# Revit family: CRUo
name_source: partatom
category: Lighting Fixtures
units: mm (PartAtom-declared; Revit-internal decimal feet)

## family parameters
Always vertical = Yes
Cut with Voids When Loaded = No
Host = Ceiling
Light Source = Yes
Maintain Annotation Orientation = No
OmniClass Number = 23.80.70.11.14.17
OmniClass Title = Direct/Indirect
Part Type = Normal
Room Calculation Point = No
Round Connector Dimension = Use Diameter
Shared = No

## types (15) — shared parameters
Color Filter = 16777215
Default Elevation = 0' - 0"
Description = LED Cleanroom Recessed with Overlapping Doorframe
Dimming Lamp Color Temperature Shift = <None>
Emit Shape Visible in Rendering = No
Housing Finish = Metal - Viscor - White
Lamp = LED
Manufacturer = Certolux By Viscor
Model = CRUo
Tilt Angle = 90.00°
URL = https://viscor.com
Voltage = 120 V

## per-type parameters (varying)
| type | Apparent Load | Assembly Code | Emit from Rectangle Length | Emit from Rectangle Width | Lamp Wattage | Length | Lens Finish | Photometric Web File | Width |
| CRUo-1X4-LED840K035LUNV-DSA | 32 VA |  | 3' - 11 3/4" | 0' - 11 3/4" | 32 VA | 3' - 11 3/4" | Acrylic - Viscor - Frosted Prismatic P12 | CRUo-1X4-LED840K035LUNV-DSA.ies | 0' - 11 3/4" |
| CRUo-2X2-LED840K035LUNV-DSA | 31 VA |  | 1' - 11 3/4" | 1' - 11 3/4" | 31 VA | 1' - 11 3/4" | Acrylic - Viscor - Frosted Prismatic P12 | CRUo-2X2-LED840K035LUNV-DSA.ies | 1' - 11 3/4" |
| CRUo-2X4-LED840K055LUNV-DSA | 45 VA |  | 3' - 11 3/4" | 1' - 11 3/4" | 45 VA | 3' - 11 3/4" | Acrylic - Viscor - Frosted Prismatic P12 | CRUo-2X4-LED840K55LUNV-DSA.IES | 1' - 11 3/4" |
| CRUo-1X4-LED840K055LUNV-DSA | 51 VA |  | 3' - 11 3/4" | 0' - 11 3/4" | 51 VA | 3' - 11 3/4" | Acrylic - Viscor - Frosted Prismatic P12 | CRUo-1X4-LED840K055LUNV-DSA.ies | 0' - 11 3/4" |
| CRUo-1X4-LED840K070LUNV-DSA | 68 VA |  | 3' - 11 3/4" | 0' - 11 3/4" | 68 VA | 3' - 11 3/4" | Acrylic - Viscor - Frosted Prismatic P12 | CRUo-1X4-LED840K070LUNV-DSA.ies | 0' - 11 3/4" |
| CRUo-1X4-LED840K100LUNV-DSA | 96 VA | D5020200 | 3' - 11 3/4" | 0' - 11 3/4" | 96 VA | 3' - 11 3/4" | Acrylic - Viscor - Frosted Prismatic P12 | CRUo-1X4-LED840K100LUNV-DSA.ies | 0' - 11 3/4" |
| CRUo-2X2-LED840K055LUNV-DSA | 50 VA |  | 1' - 11 3/4" | 1' - 11 3/4" | 50 VA | 1' - 11 3/4" | Acrylic - Viscor - Frosted Prismatic P12 | CRUo-2X2-LED840K055LUNV-DSA.ies | 1' - 11 3/4" |
| CRUo-2X2-LED840K070LUNV-DSA | 65 VA |  | 1' - 11 3/4" | 1' - 11 3/4" | 65 VA | 1' - 11 3/4" | Acrylic - Viscor - Frosted Prismatic P12 | CRUo-2X2-LED840K070LUNV-DSA.ies | 1' - 11 3/4" |
| CRUo-2X2-LED840K100LUNV-DSA | 93 VA |  | 1' - 11 3/4" | 1' - 11 3/4" | 93 VA | 1' - 11 3/4" | Acrylic - Viscor - Frosted Prismatic P12 | CRUo-2X2-LED840K100LUNV-DSA.ies | 1' - 11 3/4" |
| CRUo-2X4-LED840K070LUNV-DSA | 59 VA |  | 3' - 11 3/4" | 1' - 11 3/4" | 59 VA | 3' - 11 3/4" | Acrylic - Viscor - Frosted Prismatic P12 | CRUo-2X4-LED840K70LUNV-DSA.IES | 1' - 11 3/4" |
| CRUo-2X4-LED840K100LUNV-DSA | 80 VA |  | 3' - 11 3/4" | 1' - 11 3/4" | 80 VA | 3' - 11 3/4" | Acrylic - Viscor - Frosted Prismatic P12 | CRUo-2X4-LED840K100LUNV-DSA.ies | 1' - 11 3/4" |
| CRUo-2X4-LED840K120LUNV-DSA | 99 VA |  | 3' - 11 3/4" | 1' - 11 3/4" | 99 VA | 3' - 11 3/4" | Acrylic - Viscor - Frosted Prismatic P12 | CRUo-2X4-LED840K120LUNV-DSA.ies | 1' - 11 3/4" |
| CRUo-2X4-LED840K180LUNV-DSA | 143 VA |  | 3' - 11 3/4" | 1' - 11 3/4" | 143 VA | 3' - 11 3/4" | Acrylic - Viscor - Frosted Prismatic P12 | CRUo-2X4-LED840K180LUNV-DSA.ies | 1' - 11 3/4" |
| CRUo-2X4-LED840K240LUNV-DSA | 198 VA |  | 3' - 11 3/4" | 1' - 11 3/4" | 198 VA | 3' - 11 3/4" | Acrylic - Viscor - Frosted Prismatic P12 | CRUo-2X4-LED840K240LUNV-DSA.ies | 1' - 11 3/4" |
| CRUo-2X4-LED840K120LUNV-P103 | 99 VA |  | 3' - 11 3/4" | 1' - 11 3/4" | 99 VA | 3' - 11 3/4" | Polycarbonate - Viscor - Clear Lens | CRUo-2X4-LED840K120LUNV-P103.ies | 1' - 11 3/4" |

## geometry (parser evidence)
native form markers: Sweep x3
no freeform markers — native parametric forms only
